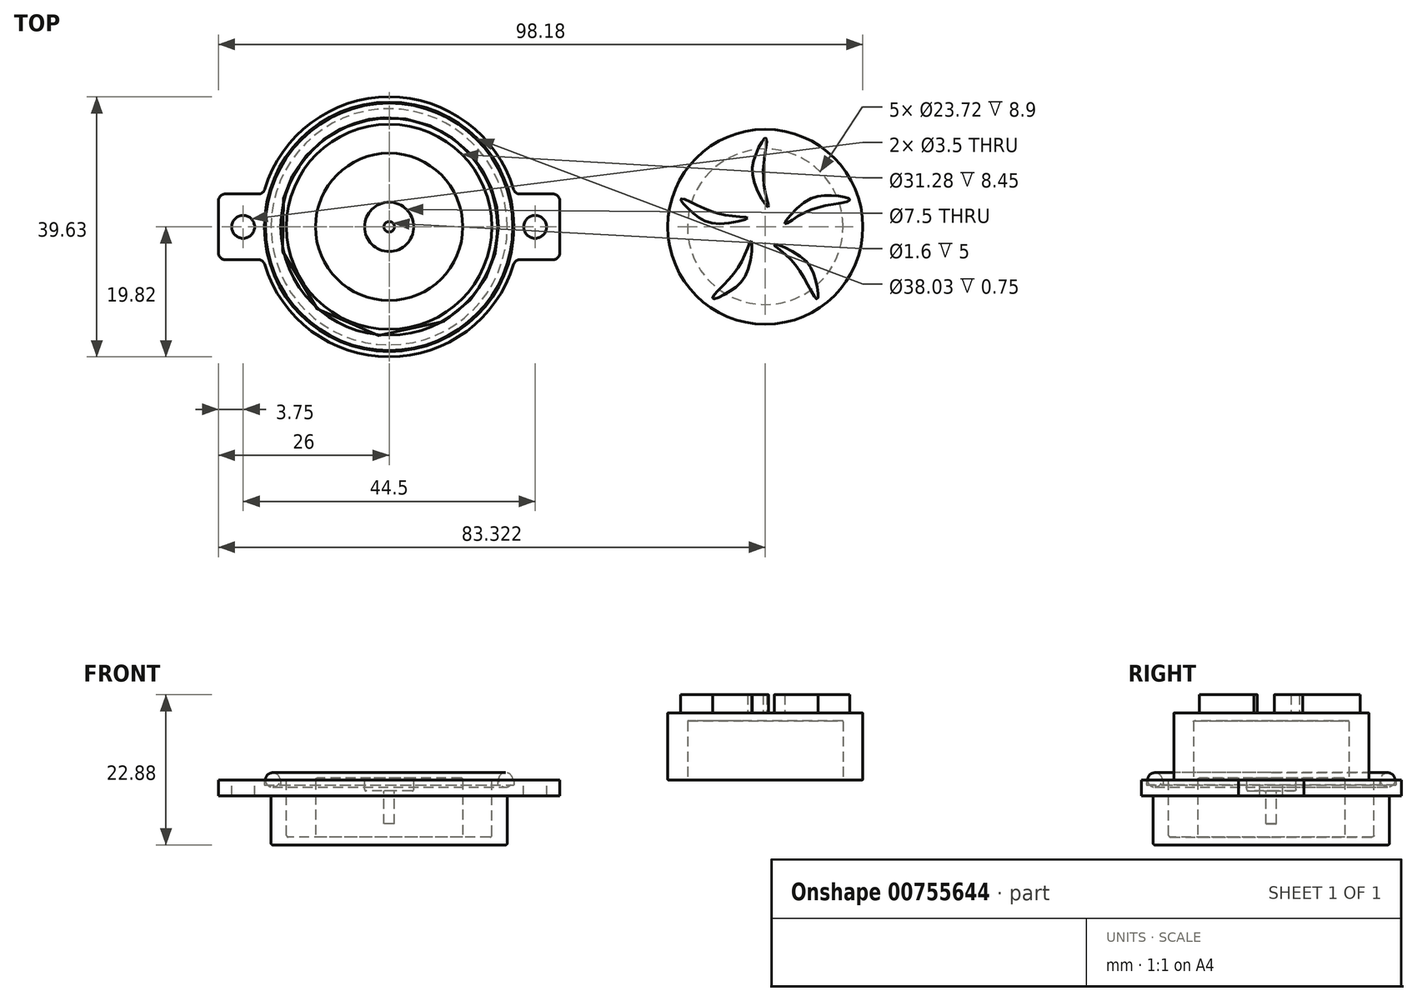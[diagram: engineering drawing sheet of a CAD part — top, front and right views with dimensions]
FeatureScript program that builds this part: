
annotation { "Feature Type Name" : "Feature", "Feature Type Description" : "" }
export const myFeature = defineFeature(function(context is Context, id is Id, definition is map)
    precondition{}
    {
        {
            var Q0;
            Q0=qCreatedBy(makeId("Top.planeOp"),FACE);
            var sketch = newSketch(context, id + "F0", { "sketchPlane" : qUnion([Q0])});
            skArc(sketch, "E0", {"start": v(-19.17, -5) * mm, "mid": v(0, -19.82) * mm, "end": v(19.17, -5) * mm});
            skLineSegment(sketch, "E1.bottom", {"start": v(26, -5) * mm, "end": v(19.17, -5) * mm});
            skLineSegment(sketch, "E1.top", {"start": v(26, 5) * mm, "end": v(19.17, 5) * mm});
            skLineSegment(sketch, "E1.left", {"start": v(26, -5) * mm, "end": v(26, 5) * mm});
            skLineSegment(sketch, "E1.right", {"start": v(-26, -5) * mm, "end": v(-26, 5) * mm});
            skLineSegment(sketch, "E2.trimOffspring", {"start": v(-19.17, -5) * mm, "end": v(-26, -5) * mm});
            skLineSegment(sketch, "E3.trimOffspring", {"start": v(-19.17, 5) * mm, "end": v(-26, 5) * mm});
            skArc(sketch, "E4.trimOffspring", {"start": v(19.17, 5) * mm, "mid": v(0, 19.82) * mm, "end": v(-19.17, 5) * mm});
            skLineSegment(sketch, "E5", {"start": v(0, -31.27) * mm, "end": v(0, 37.05) * mm, "construction": true});
            skCircle(sketch, "E6", {"center": v(-22.25, 0) * mm, "radius": 1.75 * mm});
            skLineSegment(sketch, "E7", {"start": v(-22.25, -18.72) * mm, "end": v(-22.25, 21.3) * mm, "construction": true});
            skCircle(sketch, "E8.MirrorC", {"center": v(22.25, 0) * mm, "radius": 1.75 * mm});
            skSolve(sketch);
        }
        {
            var Q0;
            Q0=makeQuery(id+"F0.imprint","IMPRINT",FACE,{"disambiguationData":[TD([[makeQuery(id+"F0.imprint","IMPRINT",EDGE,{"derivedFrom":sQuery(id+"F0.wireOp",EDGE,"E0")}),1.0]])]});
            extrude(context, id + "F1", {"entities" : qUnion([Q0]), "oppositeDirection" : true, "depth" : 2.4 * mm, "offsetDistance" : 25 * mm});
        }
        {
            var Q0;
            Q0=makeQuery(id+"F1.opExtrude","SWEPT_EDGE",EDGE,{"disambiguationData":[OSD([sQuery(id+"F0.wireOp",EDGE,"E1.bottom"),sQuery(id+"F0.wireOp",EDGE,"E1.left")])]});
            var Q1;
            Q1=makeQuery(id+"F1.opExtrude","SWEPT_EDGE",EDGE,{"disambiguationData":[OSD([sQuery(id+"F0.wireOp",EDGE,"E0"),sQuery(id+"F0.wireOp",EDGE,"E1.bottom")])]});
            var Q2;
            Q2=makeQuery(id+"F1.opExtrude","SWEPT_EDGE",EDGE,{"disambiguationData":[OSD([sQuery(id+"F0.wireOp",EDGE,"E1.top"),sQuery(id+"F0.wireOp",EDGE,"E1.left")])]});
            var Q3;
            Q3=makeQuery(id+"F1.opExtrude","SWEPT_EDGE",EDGE,{"disambiguationData":[OSD([sQuery(id+"F0.wireOp",EDGE,"E1.top"),sQuery(id+"F0.wireOp",EDGE,"E4.trimOffspring")])]});
            var Q4;
            Q4=makeQuery(id+"F1.opExtrude","SWEPT_EDGE",EDGE,{"disambiguationData":[OSD([sQuery(id+"F0.wireOp",EDGE,"E3.trimOffspring"),sQuery(id+"F0.wireOp",EDGE,"E4.trimOffspring")])]});
            var Q5;
            Q5=makeQuery(id+"F1.opExtrude","SWEPT_EDGE",EDGE,{"disambiguationData":[OSD([sQuery(id+"F0.wireOp",EDGE,"E1.right"),sQuery(id+"F0.wireOp",EDGE,"E3.trimOffspring")])]});
            var Q6;
            Q6=makeQuery(id+"F1.opExtrude","SWEPT_EDGE",EDGE,{"disambiguationData":[OSD([sQuery(id+"F0.wireOp",EDGE,"E1.right"),sQuery(id+"F0.wireOp",EDGE,"E2.trimOffspring")])]});
            var Q7;
            Q7=makeQuery(id+"F1.opExtrude","SWEPT_EDGE",EDGE,{"disambiguationData":[OSD([sQuery(id+"F0.wireOp",EDGE,"E0"),sQuery(id+"F0.wireOp",EDGE,"E2.trimOffspring")])]});
            fillet(context, id + "F2", {"entities" : qUnion([Q0, Q1, Q2, Q3, Q4, Q5, Q6, Q7]), "radius" : 1 * mm, "tangentPropagation" : true, "allowEdgeOverflow" : false});
        }
        {
            var Q0;
            Q0=makeQuery(id+"F1.opExtrude","CAP_FACE",FACE,{"disambiguationData":[OSD([sQuery(id+"F0.wireOp",EDGE,"E0"),sQuery(id+"F0.wireOp",EDGE,"E1.bottom"),sQuery(id+"F0.wireOp",EDGE,"E1.top"),sQuery(id+"F0.wireOp",EDGE,"E1.left"),sQuery(id+"F0.wireOp",EDGE,"E1.right"),sQuery(id+"F0.wireOp",EDGE,"E2.trimOffspring"),sQuery(id+"F0.wireOp",EDGE,"E3.trimOffspring"),sQuery(id+"F0.wireOp",EDGE,"E4.trimOffspring"),sQuery(id+"F0.wireOp",EDGE,"E6"),sQuery(id+"F0.wireOp",EDGE,"E8.MirrorC")])],"isStart":false});
            var sketch = newSketch(context, id + "F3", { "sketchPlane" : qUnion([Q0])});
            skCircle(sketch, "E9", {"center": v(0, 0) * mm, "radius": 18 * mm});
            skSolve(sketch);
        }
        {
            var Q0;
            Q0 = qSketchRegion(id + "F3", true);
            extrude(context, id + "F4", {"entities" : qUnion([Q0]), "operationType" : NewBodyOperationType.ADD, "depth" : 7.5 * mm, "offsetDistance" : 25 * mm});
        }
        {
            var Q0;
            Q0=makeQuery(id+"F1.opExtrude","CAP_FACE",FACE,{"disambiguationData":[OSD([sQuery(id+"F0.wireOp",EDGE,"E0"),sQuery(id+"F0.wireOp",EDGE,"E1.bottom"),sQuery(id+"F0.wireOp",EDGE,"E1.top"),sQuery(id+"F0.wireOp",EDGE,"E1.left"),sQuery(id+"F0.wireOp",EDGE,"E1.right"),sQuery(id+"F0.wireOp",EDGE,"E2.trimOffspring"),sQuery(id+"F0.wireOp",EDGE,"E3.trimOffspring"),sQuery(id+"F0.wireOp",EDGE,"E4.trimOffspring"),sQuery(id+"F0.wireOp",EDGE,"E6"),sQuery(id+"F0.wireOp",EDGE,"E8.MirrorC")])],"isStart":true});
            var sketch = newSketch(context, id + "F5", { "sketchPlane" : qUnion([Q0])});
            skCircle(sketch, "E10", {"center": v(0, 0) * mm, "radius": 15.64 * mm});
            skSolve(sketch);
        }
        {
            var Q0;
            Q0 = qSketchRegion(id + "F5", true);
            extrude(context, id + "F6", {"entities" : qUnion([Q0]), "operationType" : NewBodyOperationType.REMOVE, "oppositeDirection" : true, "depth" : 8.7 * mm, "offsetDistance" : 25 * mm});
        }
        {
            var Q0;
            Q0=makeQuery(id+"F6.boolean.opBoolean","COPY",FACE,{"derivedFrom":makeQuery(id+"F6.opExtrude","CAP_FACE",FACE,{"disambiguationData":[OSD([sQuery(id+"F5.wireOp",EDGE,"E10")])],"isStart":false})});
            var sketch = newSketch(context, id + "F7", { "sketchPlane" : qUnion([Q0])});
            skCircle(sketch, "E11", {"center": v(0, 0) * mm, "radius": 11.23 * mm});
            skSolve(sketch);
        }
        {
            var Q0;
            Q0=makeQuery(id+"F7.imprint","IMPRINT",FACE,{"disambiguationData":[TD([[makeQuery(id+"F7.imprint","IMPRINT",EDGE,{"derivedFrom":sQuery(id+"F7.wireOp",EDGE,"E11")}),1.0]])]});
            extrude(context, id + "F8", {"entities" : qUnion([Q0]), "operationType" : NewBodyOperationType.ADD, "depth" : 9 * mm, "offsetDistance" : 25 * mm});
        }
        {
            var Q0;
            Q0=makeQuery(id+"F8.opExtrude","CAP_FACE",FACE,{"disambiguationData":[OSD([sQuery(id+"F7.wireOp",EDGE,"E11")])],"isStart":false});
            var sketch = newSketch(context, id + "F9", { "sketchPlane" : qUnion([Q0])});
            skCircle(sketch, "E12", {"center": v(0, 0) * mm, "radius": 3.75 * mm});
            skSolve(sketch);
        }
        {
            var Q0;
            Q0=makeQuery(id+"F9.imprint","IMPRINT",FACE,{"disambiguationData":[TD([[makeQuery(id+"F9.imprint","IMPRINT",EDGE,{"derivedFrom":sQuery(id+"F9.wireOp",EDGE,"E12")}),1.0]])]});
            extrude(context, id + "F10", {"entities" : qUnion([Q0]), "operationType" : NewBodyOperationType.REMOVE, "oppositeDirection" : true, "depth" : 2 * mm, "offsetDistance" : 25 * mm});
        }
        {
            var Q0;
            Q0=makeQuery(id+"F10.boolean.opBoolean","COPY",FACE,{"derivedFrom":makeQuery(id+"F10.opExtrude","CAP_FACE",FACE,{"disambiguationData":[OSD([sQuery(id+"F9.wireOp",EDGE,"E12")])],"isStart":false})});
            var sketch = newSketch(context, id + "F11", { "sketchPlane" : qUnion([Q0])});
            skCircle(sketch, "E13", {"center": v(0, 0) * mm, "radius": 0.8 * mm});
            skSolve(sketch);
        }
        {
            var Q0;
            Q0=makeQuery(id+"F11.imprint","IMPRINT",FACE,{"disambiguationData":[TD([[makeQuery(id+"F11.imprint","IMPRINT",EDGE,{"derivedFrom":sQuery(id+"F11.wireOp",EDGE,"E13")}),1.0]])]});
            extrude(context, id + "F12", {"entities" : qUnion([Q0]), "operationType" : NewBodyOperationType.REMOVE, "oppositeDirection" : true, "depth" : 5 * mm, "offsetDistance" : 25 * mm});
        }
        {
            var Q0;
            Q0=makeQuery(id+"F4.opExtrude","CAP_EDGE",EDGE,{"disambiguationData":[OSD([sQuery(id+"F3.wireOp",EDGE,"E9")])],"isStart":false});
            var Q1;
            Q1=makeQuery(id+"F4.opExtrude","CAP_EDGE",EDGE,{"disambiguationData":[OSD([sQuery(id+"F3.wireOp",EDGE,"E9")])],"isStart":true});
            var Q2;
            Q2=makeQuery(id+"F6.boolean.opBoolean","COPY",EDGE,{"derivedFrom":makeQuery(id+"F6.opExtrude","CAP_EDGE",EDGE,{"disambiguationData":[OSD([sQuery(id+"F5.wireOp",EDGE,"E10")])],"isStart":false})});
            var Q3;
            Q3=makeQuery(id+"F8.opExtrude","CAP_EDGE",EDGE,{"disambiguationData":[OSD([sQuery(id+"F7.wireOp",EDGE,"E11")])],"isStart":true});
            var Q4;
            Q4=makeQuery(id+"F8.opExtrude","CAP_EDGE",EDGE,{"disambiguationData":[OSD([sQuery(id+"F7.wireOp",EDGE,"E11")])],"isStart":false});
            var Q5;
            Q5=makeQuery(id+"F10.boolean.opBoolean","COPY",EDGE,{"derivedFrom":makeQuery(id+"F10.opExtrude","CAP_EDGE",EDGE,{"disambiguationData":[OSD([sQuery(id+"F9.wireOp",EDGE,"E12")])],"isStart":true})});
            var Q6;
            Q6=makeQuery(id+"F10.boolean.opBoolean","COPY",EDGE,{"derivedFrom":makeQuery(id+"F10.opExtrude","CAP_EDGE",EDGE,{"disambiguationData":[OSD([sQuery(id+"F9.wireOp",EDGE,"E12")])],"isStart":false})});
            var Q7;
            Q7=makeQuery(id+"F12.boolean.opBoolean","COPY",EDGE,{"derivedFrom":makeQuery(id+"F12.opExtrude","CAP_EDGE",EDGE,{"disambiguationData":[OSD([sQuery(id+"F11.wireOp",EDGE,"E13")])],"isStart":true})});
            fillet(context, id + "F13", {"entities" : qUnion([Q0, Q1, Q2, Q3, Q4, Q5, Q6, Q7]), "radius" : .25 * mm, "tangentPropagation" : true, "allowEdgeOverflow" : false});
        }
        {
            var Q0;
            Q0=qCreatedBy(makeId("Right.planeOp"),FACE);
            var sketch = newSketch(context, id + "F14", { "sketchPlane" : qUnion([Q0])});
            skLineSegment(sketch, "E14.bottom", {"start": v(19.02, -0.75) * mm, "end": v(16.52, -0.75) * mm});
            skLineSegment(sketch, "E14.top", {"start": v(19.02, 0.75) * mm, "end": v(16.52, 0.75) * mm});
            skLineSegment(sketch, "E14.left", {"start": v(19.02, -0.75) * mm, "end": v(19.02, 0.75) * mm});
            skLineSegment(sketch, "E14.right", {"start": v(16.52, -0.75) * mm, "end": v(16.52, 0.75) * mm});
            skPoint(sketch, "E14.middle", {"position": v(17.77, 0) * mm});
            skSolve(sketch);
        }
        {
            var Q0;
            Q0=qCreatedBy(makeId("Right.planeOp"),FACE);
            var sketch = newSketch(context, id + "F15", { "sketchPlane" : qUnion([Q0])});
            skLineSegment(sketch, "E15", {"start": v(0, 16.9) * mm, "end": v(0, -28.64) * mm, "construction": true});
            skSolve(sketch);
        }
        {
            var Q0;
            Q0=makeQuery(id+"F14.imprint","IMPRINT",FACE,{"disambiguationData":[TD([[makeQuery(id+"F14.imprint","IMPRINT",EDGE,{"derivedFrom":sQuery(id+"F14.wireOp",EDGE,"E14.bottom")}),-1.0]])]});
            var Q1;
            Q1=sQuery(id+"F15.wireOp",EDGE,"E15");
            revolve(context, id + "F16", {"operationType" : NewBodyOperationType.REMOVE, "surfaceOperationType" : NewSurfaceOperationType.NEW, "entities" : qUnion([Q0]), "axis" : qUnion([Q1]), "revolveType" : RevolveType.FULL, "oppositeDirection" : true});
        }
        {
            var Q0;
            Q0=qCreatedBy(makeId("Top.planeOp"),FACE);
            var sketch = newSketch(context, id + "F17", { "sketchPlane" : qUnion([Q0])});
            skCircle(sketch, "E16", {"center": v(0, 0) * mm, "radius": 17.75 * mm, "construction": true});
            skSolve(sketch);
        }
        {
            var Q0;
            Q0=qCreatedBy(makeId("Front.planeOp"),FACE);
            var sketch = newSketch(context, id + "F18", { "sketchPlane" : qUnion([Q0])});
            skCircle(sketch, "E17", {"center": v(17.75, 0) * mm, "radius": 1.1 * mm});
            skLineSegment(sketch, "E18", {"start": v(0, 22.33) * mm, "end": v(0, -30.33) * mm, "construction": true});
            skSolve(sketch);
        }
        {
            var Q0;
            Q0=qCreatedBy(makeId("Front.planeOp"),FACE);
            var sketch = newSketch(context, id + "F19", { "sketchPlane" : qUnion([Q0])});
            skLineSegment(sketch, "E19", {"start": v(0, 29.22) * mm, "end": v(0, -36.7) * mm, "construction": true});
            skSolve(sketch);
        }
        {
            var Q0;
            Q0=makeQuery(id+"F18.imprint","IMPRINT",FACE,{"disambiguationData":[TD([[makeQuery(id+"F18.imprint","IMPRINT",EDGE,{"derivedFrom":sQuery(id+"F18.wireOp",EDGE,"E17")}),1.0]])]});
            var Q1;
            Q1=sQuery(id+"F19.wireOp",EDGE,"E19");
            revolve(context, id + "F20", {"surfaceOperationType" : NewSurfaceOperationType.NEW, "entities" : qUnion([Q0]), "axis" : qUnion([Q1]), "revolveType" : RevolveType.FULL});
        }
        {
            var Q0;
            Q0=qCreatedBy(makeId("Top.planeOp"),FACE);
            var sketch = newSketch(context, id + "F21", { "sketchPlane" : qUnion([Q0])});
            skCircle(sketch, "E20", {"center": v(57.32, 0) * mm, "radius": 14.86 * mm});
            skSolve(sketch);
        }
        {
            var Q0;
            Q0 = qSketchRegion(id + "F21", true);
            extrude(context, id + "F22", {"entities" : qUnion([Q0]), "depth" : 10.23 * mm, "offsetDistance" : 25 * mm});
        }
        {
            var Q0;
            Q0=makeQuery(id+"F22.opExtrude","CAP_FACE",FACE,{"disambiguationData":[OSD([sQuery(id+"F21.wireOp",EDGE,"E20")])],"isStart":true});
            var sketch = newSketch(context, id + "F23", { "sketchPlane" : qUnion([Q0])});
            skCircle(sketch, "E21", {"center": v(57.32, 0) * mm, "radius": 11.86 * mm});
            skSolve(sketch);
        }
        {
            var Q0;
            Q0=makeQuery(id+"F23.imprint","IMPRINT",FACE,{"disambiguationData":[TD([[makeQuery(id+"F23.imprint","IMPRINT",EDGE,{"derivedFrom":sQuery(id+"F23.wireOp",EDGE,"E21")}),1.0]])]});
            extrude(context, id + "F24", {"entities" : qUnion([Q0]), "operationType" : NewBodyOperationType.REMOVE, "oppositeDirection" : true, "depth" : 9 * mm, "offsetDistance" : 25 * mm});
        }
        {
            var Q0;
            Q0=makeQuery(id+"F22.opExtrude","CAP_EDGE",EDGE,{"disambiguationData":[OSD([sQuery(id+"F21.wireOp",EDGE,"E20")])],"isStart":false});
            var Q1;
            Q1=makeQuery(id+"F22.opExtrude","CAP_EDGE",EDGE,{"disambiguationData":[OSD([sQuery(id+"F21.wireOp",EDGE,"E20")])],"isStart":true});
            var Q2;
            Q2=makeQuery(id+"F24.boolean.opBoolean","COPY",EDGE,{"derivedFrom":makeQuery(id+"F24.opExtrude","CAP_EDGE",EDGE,{"disambiguationData":[OSD([sQuery(id+"F23.wireOp",EDGE,"E21")])],"isStart":true})});
            var Q3;
            Q3=makeQuery(id+"F24.boolean.opBoolean","COPY",EDGE,{"derivedFrom":makeQuery(id+"F24.opExtrude","CAP_EDGE",EDGE,{"disambiguationData":[OSD([sQuery(id+"F23.wireOp",EDGE,"E21")])],"isStart":false})});
            fillet(context, id + "F25", {"entities" : qUnion([Q0, Q1, Q2, Q3]), "radius" : .1 * mm, "tangentPropagation" : true, "allowEdgeOverflow" : false});
        }
        {
            var Q0;
            Q0=qCreatedBy(makeId("Front.planeOp"),FACE);
            var sketch = newSketch(context, id + "F26", { "sketchPlane" : qUnion([Q0])});
            skLineSegment(sketch, "E22", {"start": v(57.32, 44.93) * mm, "end": v(57.32, -32.5) * mm, "construction": true});
            skSolve(sketch);
        }
        {
            var Q0;
            Q0=makeQuery(id+"F22.opExtrude","CAP_FACE",FACE,{"disambiguationData":[OSD([sQuery(id+"F21.wireOp",EDGE,"E20")])],"isStart":false});
            var sketch = newSketch(context, id + "F27", { "sketchPlane" : qUnion([Q0])});
            skFitSpline(sketch, "E23", {"points": [v(60.3, 0.48) * mm, v(63.29, 3.74) * mm, v(67.49, 4.77) * mm, v(70.17, 4.23) * mm, v(70.12, 3.98) * mm, v(66.53, 3.23) * mm, v(62.22, 1.56) * mm, v(60.3, 0.48) * mm]});
            skSolve(sketch);
        }
        {
            var Q0;
            Q0=makeQuery(id+"F27.imprint","IMPRINT",FACE,{"disambiguationData":[TD([[makeQuery(id+"F27.imprint","IMPRINT",EDGE,{"derivedFrom":sQuery(id+"F27.wireOp",EDGE,"E23")}),-1.0]])]});
            extrude(context, id + "F28", {"entities" : qUnion([Q0]), "operationType" : NewBodyOperationType.ADD, "depth" : 2.75 * mm, "offsetDistance" : 25 * mm});
        }
        {
            var Q0;
            Q0=makeQuery(id+"F22.opExtrude","SWEPT_BODY",BODY,{"disambiguationData":[OSD([sQuery(id+"F21.wireOp",EDGE,"E20")])]});
            var Q1;
            Q1=sQuery(id+"F26.wireOp",EDGE,"E22");
            circularPattern(context, id + "F29", {"operationType" : NewBodyOperationType.ADD, "entities" : qUnion([Q0]), "axis" : qUnion([Q1]), "angle" : 360 * degree, "instanceCount" : 5, "equalSpace" : true});
        }
    });
